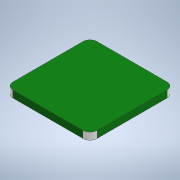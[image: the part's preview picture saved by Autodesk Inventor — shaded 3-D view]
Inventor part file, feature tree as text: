
AUTODESK INVENTOR PART (.ipt)
format: ipt  version: 2022.3 (Build 263350000, 350)  size: 113,152 bytes
history: native  units: mm
features: extrude x1, fillet x1, sketch x1
ambient origin geometry x8: Origin, YZ Plane, XZ Plane, XY Plane, X Axis, Y Axis, Z Axis, Center Point
bodies: Solid1 (feature_tree)
feature tree (3):
  extrude  "Extrusion1"  Depth=24.0mm
  fillet  "Fillet1"  Radius=2.0mm
  sketch  "Sketch1"  dims[d0=24.0mm d1=24.0mm d2=2.0mm d3=0.0mm d4=2.0mm]
